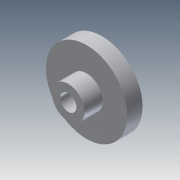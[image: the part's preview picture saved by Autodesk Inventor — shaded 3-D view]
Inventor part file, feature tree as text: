
AUTODESK INVENTOR PART (.ipt)
format: ipt  version: 2013 (Build 170138000, 138)  size: 121,856 bytes
history: native  units: mm
features: sketch x8, extrude x7
ambient origin geometry x8: Origin, YZ Plane, XZ Plane, XY Plane, X Axis, Y Axis, Z Axis, Center Point
bodies: Solid1 (feature_tree)
feature tree (15):
  sketch  "Sketch1"  dims[d0=20.0mm d1=1.8mm d2=0.0mm]
  sketch  "Sketch2"  dims[d3=7.0mm d4=5.0mm]
  extrude  "Extrusion1"  Depth=1.8mm TaperAngle=0.0deg
  extrude  "Extrusion2"  Depth=5.0mm
  extrude  "Extrusion3"  Depth=6.3mm
  extrude  "Extrusion4"  Depth=2.4mm TaperAngle=0.0deg
  extrude  "Extrusion5"  Depth=3.0mm
  extrude  "Extrusion6"  Depth=1.8mm TaperAngle=0.0deg
  extrude  "Extrusion7"  Depth=8.0mm
  sketch  "Sketch3"  dims[d5=2.4mm d6=0.0mm d7=6.3mm]
  sketch  "Sketch4"  dims[d8=3.0mm d9=2.4mm d10=0.0mm]
  sketch  "Sketch5"  dims[d11=6.3mm d12=3.0mm]
  sketch  "Sketch6"  dims[d13=2.0mm d14=0.0mm d15=1.8mm d16=0.0mm]
  sketch  "Sketch7"  dims[d17=2.0mm d18=0.0mm d19=8.0mm]
  sketch  "Sketch8"  dims[d20=4.0mm d21=4.5mm d22=0.0mm]
